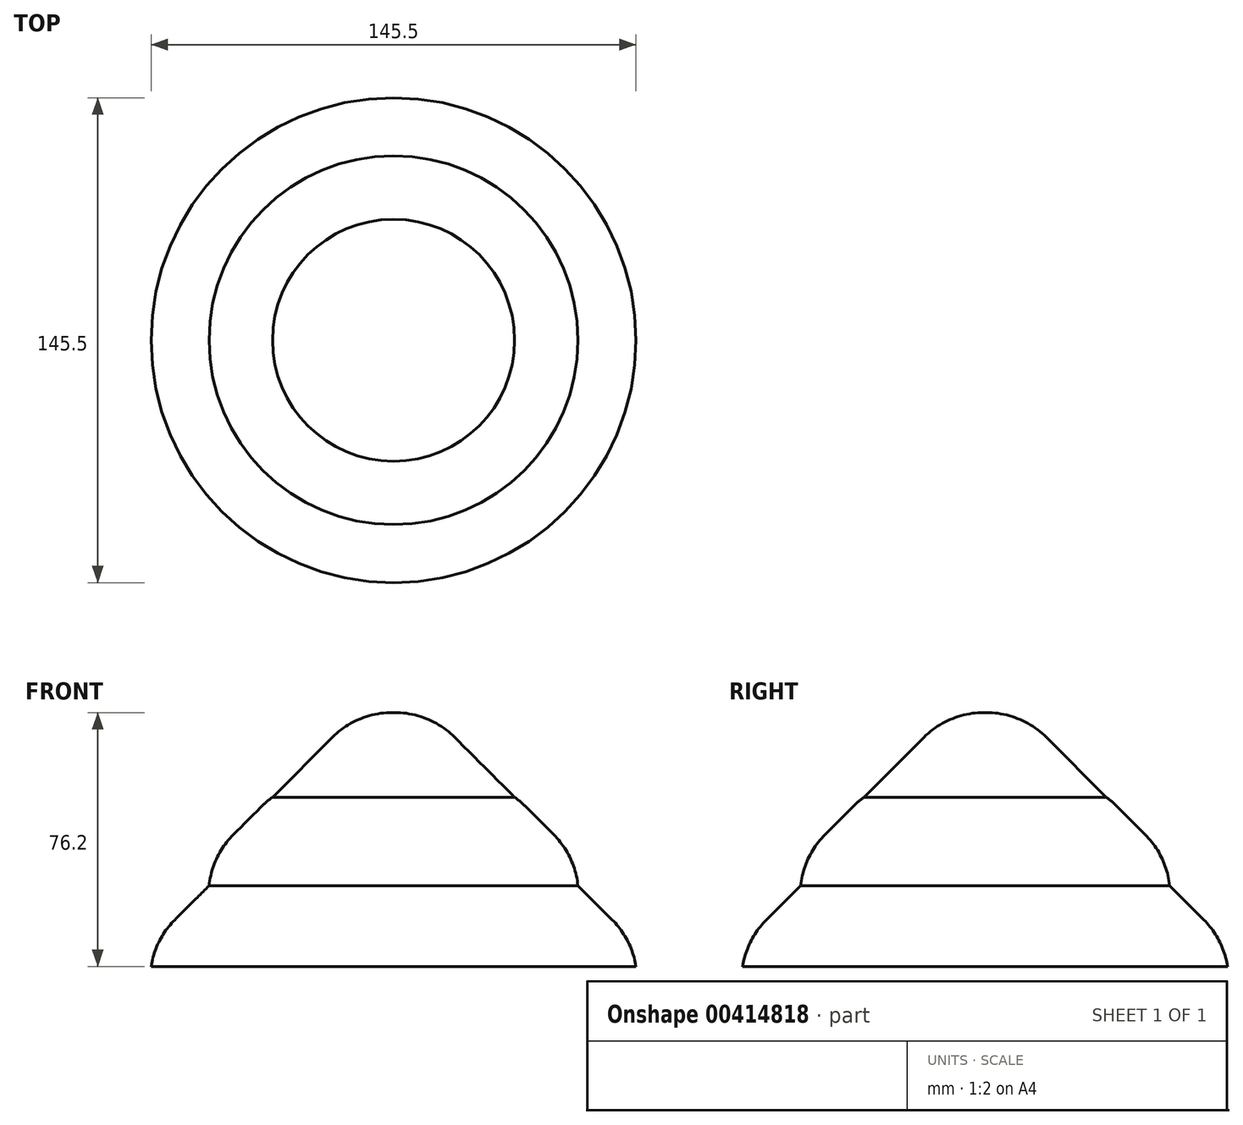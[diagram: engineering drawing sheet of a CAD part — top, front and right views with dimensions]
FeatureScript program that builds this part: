
annotation { "Feature Type Name" : "Feature", "Feature Type Description" : "" }
export const myFeature = defineFeature(function(context is Context, id is Id, definition is map)
    precondition{}
    {
        {
            var Q0;
            Q0=qCreatedBy(makeId("Top.planeOp"),FACE);
            var sketch = newSketch(context, id + "F0", { "sketchPlane" : qUnion([Q0])});
            skCircle(sketch, "E0", {"center": v(0, 0) * mm, "radius": 36.31 * mm});
            skCircle(sketch, "E1", {"center": v(0, 0) * mm, "radius": 55.34 * mm});
            skCircle(sketch, "E2", {"center": v(0, 0) * mm, "radius": 72.75 * mm});
            skSolve(sketch);
        }
        {
            var Q0;
            Q0=makeQuery(id+"F0.imprint","IMPRINT",FACE,{"disambiguationData":[TD([[makeQuery(id+"F0.imprint","IMPRINT",EDGE,{"derivedFrom":sQuery(id+"F0.wireOp",EDGE,"E0")}),1.0]])]});
            extrude(context, id + "F1", {"entities" : qUnion([Q0]), "depth" : 76.2 * mm});
        }
        {
            var Q0;
            Q0=makeQuery(id+"F0.imprint","IMPRINT",FACE,{"disambiguationData":[TD([[makeQuery(id+"F0.imprint","IMPRINT",EDGE,{"derivedFrom":sQuery(id+"F0.wireOp",EDGE,"E0")}),-1.0]])]});
            extrude(context, id + "F2", {"entities" : qUnion([Q0]), "operationType" : NewBodyOperationType.ADD, "depth" : 50.8 * mm});
        }
        {
            var Q0;
            Q0=makeQuery(id+"F0.imprint","IMPRINT",FACE,{"disambiguationData":[TD([[makeQuery(id+"F0.imprint","IMPRINT",EDGE,{"derivedFrom":sQuery(id+"F0.wireOp",EDGE,"E1")}),-1.0]])]});
            extrude(context, id + "F3", {"entities" : qUnion([Q0]), "operationType" : NewBodyOperationType.ADD, "depth" : 25.4 * mm});
        }
        {
            var Q0;
            Q0=makeQuery(id+"F1.opExtrude","CAP_FACE",FACE,{"disambiguationData":[OSD([sQuery(id+"F0.wireOp",EDGE,"E0")])],"isStart":false});
            chamfer(context, id + "F4", {"entities" : qUnion([Q0]), "width" : 25.4 * mm, "tangentPropagation" : true});
        }
        {
            var Q0;
            Q0=makeQuery(id+"F3.opExtrude","CAP_EDGE",EDGE,{"disambiguationData":[OSD([sQuery(id+"F0.wireOp",EDGE,"E2")])],"isStart":false});
            var Q1;
            Q1=makeQuery(id+"F2.opExtrude","CAP_EDGE",EDGE,{"disambiguationData":[OSD([sQuery(id+"F0.wireOp",EDGE,"E1")])],"isStart":false});
            chamfer(context, id + "F5", {"entities" : qUnion([Q0, Q1]), "width" : 18.54 * mm, "tangentPropagation" : true});
        }
        {
            var Q0;
            {var subQ0=sQuery(id+"F0.wireOp",EDGE,"E0");Q0=makeQuery(id+"F4.opChamfer","BLEND_EDGE",EDGE,{"blendedFrom":[makeQuery(id+"F1.opExtrude","CAP_EDGE",EDGE,{"disambiguationData":[OSD([subQ0])],"isStart":false}),makeQuery(id+"F1.opExtrude","CAP_FACE",FACE,{"disambiguationData":[OSD([subQ0])],"isStart":false})],"blendedInto":[makeQuery(id+"F1.opExtrude","CAP_FACE",FACE,{"disambiguationData":[OSD([subQ0])],"isStart":false})]});}
            var Q1;
            {var subQ0=sQuery(id+"F0.wireOp",EDGE,"E1");Q1=makeQuery(id+"F5.opChamfer","BLEND_EDGE",EDGE,{"blendedFrom":[makeQuery(id+"F2.opExtrude","CAP_EDGE",EDGE,{"disambiguationData":[OSD([subQ0])],"isStart":false}),makeQuery(id+"F2.opExtrude","SWEPT_FACE",FACE,{"disambiguationData":[OSD([subQ0])]})],"blendedInto":[makeQuery(id+"F2.opExtrude","SWEPT_FACE",FACE,{"disambiguationData":[OSD([subQ0])]})]});}
            var Q2;
            {var subQ0=sQuery(id+"F0.wireOp",EDGE,"E2");Q2=makeQuery(id+"F5.opChamfer","BLEND_EDGE",EDGE,{"blendedFrom":[makeQuery(id+"F3.opExtrude","CAP_EDGE",EDGE,{"disambiguationData":[OSD([subQ0])],"isStart":false}),makeQuery(id+"F3.opExtrude","SWEPT_FACE",FACE,{"disambiguationData":[OSD([subQ0])]})],"blendedInto":[makeQuery(id+"F3.opExtrude","SWEPT_FACE",FACE,{"disambiguationData":[OSD([subQ0])]})]});}
            var Q3;
            {var subQ0=sQuery(id+"F0.wireOp",EDGE,"E1");Q3=makeQuery(id+"F5.opChamfer","BLEND_EDGE",EDGE,{"blendedFrom":[makeQuery(id+"F2.opExtrude","CAP_EDGE",EDGE,{"disambiguationData":[OSD([subQ0])],"isStart":false}),makeQuery(id+"F2.opExtrude","CAP_FACE",FACE,{"disambiguationData":[OSD([sQuery(id+"F0.wireOp",EDGE,"E0"),subQ0])],"isStart":false})],"blendedInto":[makeQuery(id+"F2.opExtrude","CAP_FACE",FACE,{"disambiguationData":[OSD([sQuery(id+"F0.wireOp",EDGE,"E0"),subQ0])],"isStart":false})]});}
            fillet(context, id + "F6", {"entities" : qUnion([Q0, Q1, Q2, Q3]), "radius" : 25.4 * mm, "tangentPropagation" : true, "allowEdgeOverflow" : false});
        }
    });
